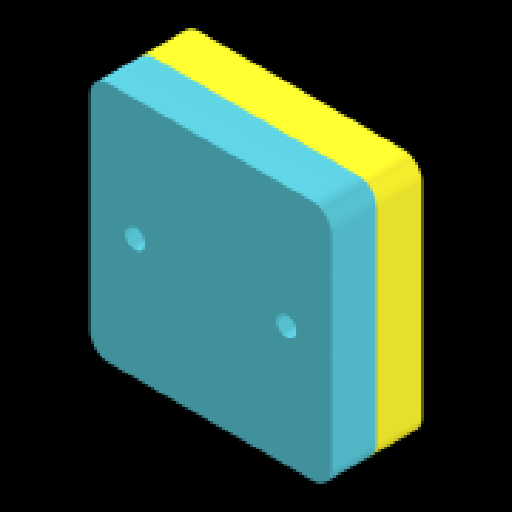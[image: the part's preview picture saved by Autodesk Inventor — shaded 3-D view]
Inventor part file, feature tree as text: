
AUTODESK INVENTOR PART (.ipt)
format: ipt  version: 2024 (Build 280153000, 153)  size: 870,400 bytes
history: native  units: mm (DEFAULTED — no unit token found)
features: other x20, sketch x6, extrude x5, reference x5, fillet x2, plane x1, hole x1, revolve x1, chamfer x1
ambient origin geometry x1: Ursprung
bodies: Volumenkörper2 (feature_tree)
feature tree (42):
  other  "IM1_Matchboxscope_plate_3"
  other  "Blöcke"
  sketch  "Skizze2"  dims[d29=4.0mm d30=-0.436332mm d31=0.436332mm]
  extrude  "Extrusion1"  Depth=4.0mm
  extrude  "Extrusion2"  Depth=7.0mm
  plane  "Arbeitsebene1"
  extrude  "Extrusion3"  Depth=2.0mm
  fillet  "Rundung1"  [1 undecoded]
  fillet  "Rundung2"  Radius=0.436332mm
  extrude  "Extrusion4"  Depth=0.3mm
  other  "Kombinieren1"
  other  "Trennen1"
  hole  "Bohrung1"  [1 undecoded]
  revolve  "Umdrehung1"
  extrude  "Extrusion10"  Depth=4.0mm
  chamfer  "Fasen2"  Angle=90.0deg  [1 undecoded]
  other  "YZ-Ebene"
  other  "XZ-Ebene"
  other  "XY-Ebene"
  other  "X-Achse"
  other  "Y-Achse"
  other  "Z-Achse"
  other  "Mittelpunkt"
  other  "PlateShape-Input-blk"
  sketch  "Skizze3"  dims[d32=7.0mm d33=0.436332mm]
  sketch  "Skizze4"  dims[d34=2.0mm d35=2.0mm d36=0.436332mm d37=-4.0mm d38=0.0mm d39=0.436332mm]
  sketch  "Skizze9"  dims[d40=2.0mm d41=0.3mm]
  reference  "Referenz5"
  reference  "Referenz6"
  reference  "Referenz7"
  reference  "Referenz8"
  sketch  "Skizze10"  dims[d42=3.0mm d43=-0.872665mm d46=24.0mm d47=0.0mm]
  sketch  "Skizze11"  dims[d79=5.3mm d80=6.0mm d81=4.0mm d82=2.0mm d83=90.0deg d84=8.0mm d85=20.594885mm d86=30.0mm d87=90.0deg d88=2.662285mm d89=8.975979mm d90=8.975979mm d91=8.975979mm d92=1.783339mm d94=0.89167mm d95=-7.853982mm d96=8.975979mm d97=40.0mm d98=0.5mm d99=2.0mm d100=45.0deg d61=0.0mm d62=0.0mm d63=0.0mm]
  reference  "Referenz9"
  other  "PlateShape-Input-blk:1"
  other  "IM1-MoldTop"
  other  "IM1-MoldBottom"
  parser-record x1  (decoder bookkeeping rows leaked as tree rows — omitted from the tree; the rows remain in map.json)
  other  "IM1_Matchboxscope_plate_3 MB bg.iam"
  other  "MicroPlast-MB-BG:1"
  other  "MP-plate movable:1"
  other  "MP-Mould Mount:1"
note: 3 required parameter values undecoded (feature->parameter linkage not recoverable at this tier; creation-order binding heuristic only, values carry confidence <= 0.55)
note: 1 file-system path scrubbed to <path> (originals preserved in map.json)
